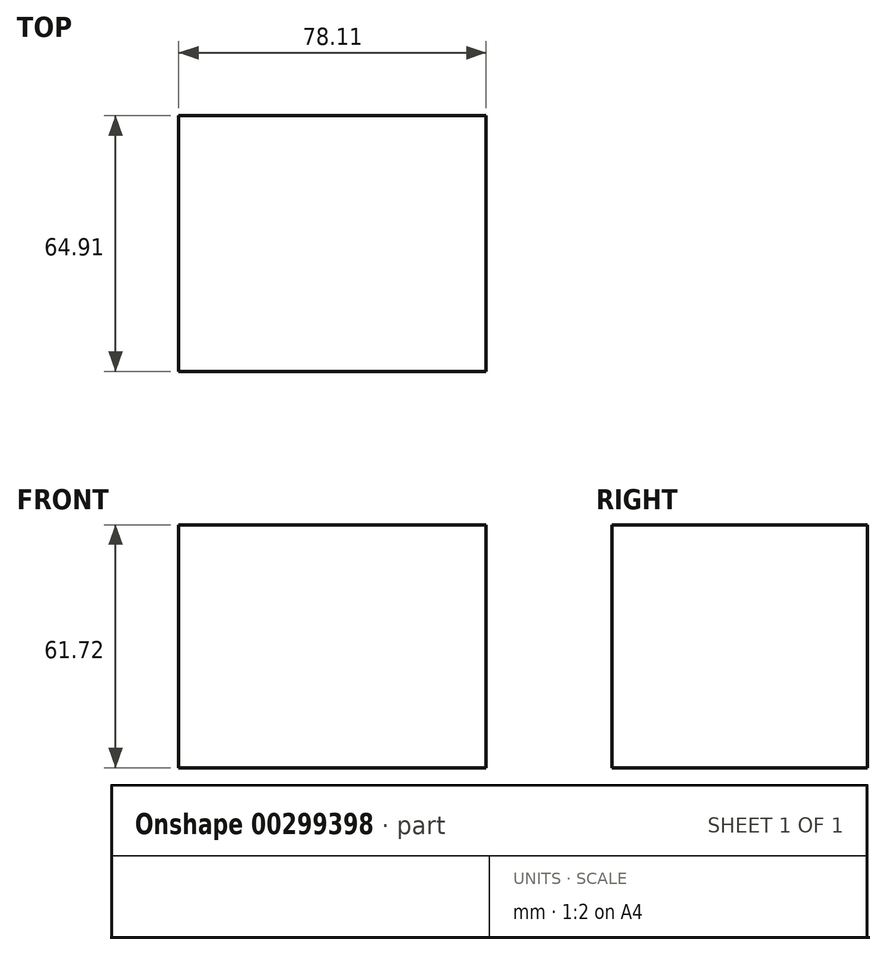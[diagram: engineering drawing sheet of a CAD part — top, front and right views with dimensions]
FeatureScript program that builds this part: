
annotation { "Feature Type Name" : "Feature", "Feature Type Description" : "" }
export const myFeature = defineFeature(function(context is Context, id is Id, definition is map)
    precondition{}
    {
        {
            var Q0;
            Q0=qCreatedBy(makeId("Top.planeOp"),FACE);
            var sketch = newSketch(context, id + "F0", { "sketchPlane" : qUnion([Q0])});
            skLineSegment(sketch, "E0.bottom", {"start": v(-26.57, 21.45) * mm, "end": v(51.54, 21.45) * mm});
            skLineSegment(sketch, "E0.top", {"start": v(-26.57, -43.46) * mm, "end": v(51.54, -43.46) * mm});
            skLineSegment(sketch, "E0.left", {"start": v(-26.57, 21.45) * mm, "end": v(-26.57, -43.46) * mm});
            skLineSegment(sketch, "E0.right", {"start": v(51.54, 21.45) * mm, "end": v(51.54, -43.46) * mm});
            skSolve(sketch);
        }
        {
            var Q0;
            Q0 = qSketchRegion(id + "F0", true);
            extrude(context, id + "F1", {"entities" : qUnion([Q0]), "depth" : 61.72 * mm});
        }
    });
